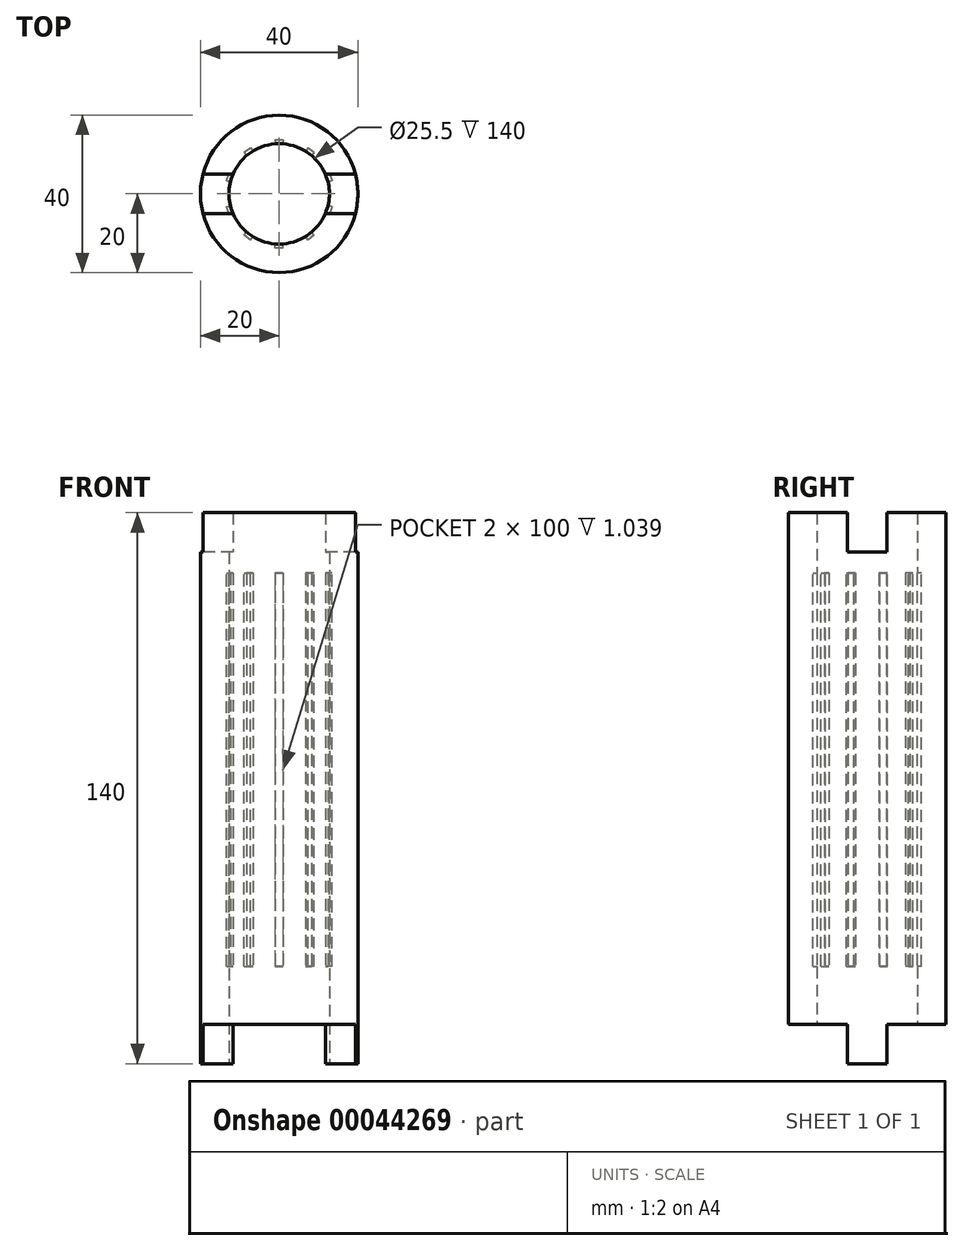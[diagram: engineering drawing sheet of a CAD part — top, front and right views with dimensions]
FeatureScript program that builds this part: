
annotation { "Feature Type Name" : "Feature", "Feature Type Description" : "" }
export const myFeature = defineFeature(function(context is Context, id is Id, definition is map)
    precondition{}
    {
        {
            var Q0;
            Q0=qCreatedBy(makeId("Top.planeOp"),FACE);
            var sketch = newSketch(context, id + "F0", { "sketchPlane" : qUnion([Q0])});
            skCircle(sketch, "E0", {"center": v(0, 0) * mm, "radius": 20 * mm});
            skCircle(sketch, "E1", {"center": v(0, 0) * mm, "radius": 12.75 * mm});
            skSolve(sketch);
        }
        {
            var Q0;
            Q0=makeQuery(id+"F0.imprint","IMPRINT",FACE,{"disambiguationData":[TD([[makeQuery(id+"F0.imprint","IMPRINT",EDGE,{"derivedFrom":sQuery(id+"F0.wireOp",EDGE,"E0")}),1.0]])]});
            var Q1;
            Q1=sQuery(id+"F0.wireOp",EDGE,"E0");
            extrude(context, id + "F1", {"entities" : qUnion([Q0]), "surfaceEntities" : qUnion([Q1]), "endBound" : BoundingType.SYMMETRIC, "depth" : 200 * mm});
        }
        {
            var Q0;
            Q0=qCreatedBy(makeId("Right.planeOp"),FACE);
            var sketch = newSketch(context, id + "F2", { "sketchPlane" : qUnion([Q0])});
            skLineSegment(sketch, "E2.bottom", {"start": v(-30, 65.34) * mm, "end": v(-5, 65.34) * mm});
            skLineSegment(sketch, "E2.top", {"start": v(-30, -64.66) * mm, "end": v(-5, -64.66) * mm});
            skLineSegment(sketch, "E2.left", {"start": v(-30, 65.34) * mm, "end": v(-30, -64.66) * mm});
            skLineSegment(sketch, "E2.right", {"start": v(30, 65.34) * mm, "end": v(30, -64.66) * mm});
            skLineSegment(sketch, "E3.top", {"start": v(-5, -74.66) * mm, "end": v(5, -74.66) * mm});
            skLineSegment(sketch, "E3.left", {"start": v(-5, -64.66) * mm, "end": v(-5, -74.66) * mm});
            skLineSegment(sketch, "E3.right", {"start": v(5, -64.66) * mm, "end": v(5, -74.66) * mm});
            skLineSegment(sketch, "E4.top", {"start": v(5, 55.34) * mm, "end": v(-5, 55.34) * mm});
            skLineSegment(sketch, "E4.left", {"start": v(5, 65.34) * mm, "end": v(5, 55.34) * mm});
            skLineSegment(sketch, "E4.right", {"start": v(-5, 65.34) * mm, "end": v(-5, 55.34) * mm});
            skLineSegment(sketch, "E5.trimOffspring", {"start": v(5, 65.34) * mm, "end": v(30, 65.34) * mm});
            skLineSegment(sketch, "E6.trimOffspring", {"start": v(5, -64.66) * mm, "end": v(30, -64.66) * mm});
            skSolve(sketch);
        }
        {
            var Q0;
            Q0=makeQuery(id+"F2.imprint","IMPRINT",FACE,{"disambiguationData":[TD([[makeQuery(id+"F2.imprint","IMPRINT",EDGE,{"derivedFrom":sQuery(id+"F2.wireOp",EDGE,"E2.bottom")}),-1.0]])]});
            extrude(context, id + "F3", {"entities" : qUnion([Q0]), "operationType" : NewBodyOperationType.INTERSECT, "endBound" : BoundingType.SYMMETRIC, "depth" : 50 * mm});
        }
        {
            var Q0;
            Q0=qCreatedBy(makeId("Top.planeOp"),FACE);
            var sketch = newSketch(context, id + "F4", { "sketchPlane" : qUnion([Q0])});
            skLineSegment(sketch, "E7.bottom", {"start": v(-1, 13.75) * mm, "end": v(1, 13.75) * mm});
            skLineSegment(sketch, "E7.top", {"start": v(-1, 11.75) * mm, "end": v(1, 11.75) * mm});
            skLineSegment(sketch, "E7.left", {"start": v(-1, 13.75) * mm, "end": v(-1, 11.75) * mm});
            skLineSegment(sketch, "E7.right", {"start": v(1, 13.75) * mm, "end": v(1, 11.75) * mm});
            skLineSegment(sketch, "E8.1.0", {"start": v(-7.27, 11.71) * mm, "end": v(-6.1, 10.1) * mm});
            skLineSegment(sketch, "E8.1.1", {"start": v(-8.9, 10.54) * mm, "end": v(-7.27, 11.71) * mm});
            skLineSegment(sketch, "E8.1.2", {"start": v(-8.9, 10.54) * mm, "end": v(-7.72, 8.92) * mm});
            skLineSegment(sketch, "E8.1.3", {"start": v(-7.72, 8.92) * mm, "end": v(-6.1, 10.1) * mm});
            skLineSegment(sketch, "E8.2.0", {"start": v(-12.77, 5.2) * mm, "end": v(-10.87, 4.58) * mm});
            skLineSegment(sketch, "E8.2.1", {"start": v(-13.39, 3.3) * mm, "end": v(-12.77, 5.2) * mm});
            skLineSegment(sketch, "E8.2.2", {"start": v(-13.39, 3.3) * mm, "end": v(-11.48, 2.68) * mm});
            skLineSegment(sketch, "E8.2.3", {"start": v(-11.48, 2.68) * mm, "end": v(-10.87, 4.58) * mm});
            skLineSegment(sketch, "E8.3.0", {"start": v(-13.39, -3.3) * mm, "end": v(-11.48, -2.68) * mm});
            skLineSegment(sketch, "E8.3.1", {"start": v(-12.77, -5.2) * mm, "end": v(-13.39, -3.3) * mm});
            skLineSegment(sketch, "E8.3.2", {"start": v(-12.77, -5.2) * mm, "end": v(-10.87, -4.58) * mm});
            skLineSegment(sketch, "E8.3.3", {"start": v(-10.87, -4.58) * mm, "end": v(-11.48, -2.68) * mm});
            skLineSegment(sketch, "E8.4.0", {"start": v(-8.9, -10.54) * mm, "end": v(-7.72, -8.92) * mm});
            skLineSegment(sketch, "E8.4.1", {"start": v(-7.27, -11.71) * mm, "end": v(-8.9, -10.54) * mm});
            skLineSegment(sketch, "E8.4.2", {"start": v(-7.27, -11.71) * mm, "end": v(-6.1, -10.1) * mm});
            skLineSegment(sketch, "E8.4.3", {"start": v(-6.1, -10.1) * mm, "end": v(-7.72, -8.92) * mm});
            skLineSegment(sketch, "E8.5.0", {"start": v(-1, -13.75) * mm, "end": v(-1, -11.75) * mm});
            skLineSegment(sketch, "E8.5.1", {"start": v(1, -13.75) * mm, "end": v(-1, -13.75) * mm});
            skLineSegment(sketch, "E8.5.2", {"start": v(1, -13.75) * mm, "end": v(1, -11.75) * mm});
            skLineSegment(sketch, "E8.5.3", {"start": v(1, -11.75) * mm, "end": v(-1, -11.75) * mm});
            skLineSegment(sketch, "E8.6.0", {"start": v(7.27, -11.71) * mm, "end": v(6.1, -10.1) * mm});
            skLineSegment(sketch, "E8.6.1", {"start": v(8.9, -10.54) * mm, "end": v(7.27, -11.71) * mm});
            skLineSegment(sketch, "E8.6.2", {"start": v(8.9, -10.54) * mm, "end": v(7.72, -8.92) * mm});
            skLineSegment(sketch, "E8.6.3", {"start": v(7.72, -8.92) * mm, "end": v(6.1, -10.1) * mm});
            skLineSegment(sketch, "E8.7.0", {"start": v(12.77, -5.2) * mm, "end": v(10.87, -4.58) * mm});
            skLineSegment(sketch, "E8.7.1", {"start": v(13.39, -3.3) * mm, "end": v(12.77, -5.2) * mm});
            skLineSegment(sketch, "E8.7.2", {"start": v(13.39, -3.3) * mm, "end": v(11.48, -2.68) * mm});
            skLineSegment(sketch, "E8.7.3", {"start": v(11.48, -2.68) * mm, "end": v(10.87, -4.58) * mm});
            skLineSegment(sketch, "E8.8.0", {"start": v(13.39, 3.3) * mm, "end": v(11.48, 2.68) * mm});
            skLineSegment(sketch, "E8.8.1", {"start": v(12.77, 5.2) * mm, "end": v(13.39, 3.3) * mm});
            skLineSegment(sketch, "E8.8.2", {"start": v(12.77, 5.2) * mm, "end": v(10.87, 4.58) * mm});
            skLineSegment(sketch, "E8.8.3", {"start": v(10.87, 4.58) * mm, "end": v(11.48, 2.68) * mm});
            skLineSegment(sketch, "E8.9.0", {"start": v(8.9, 10.54) * mm, "end": v(7.72, 8.92) * mm});
            skLineSegment(sketch, "E8.9.1", {"start": v(7.27, 11.71) * mm, "end": v(8.9, 10.54) * mm});
            skLineSegment(sketch, "E8.9.2", {"start": v(7.27, 11.71) * mm, "end": v(6.1, 10.1) * mm});
            skLineSegment(sketch, "E8.9.3", {"start": v(6.1, 10.1) * mm, "end": v(7.72, 8.92) * mm});
            skPoint(sketch, "E8.center", {"position": v(0, 0) * mm});
            skSolve(sketch);
        }
        {
            var Q0;
            Q0=qSketchRegion(id+"F4",true);
            extrude(context, id + "F5", {"entities" : qUnion([Q0]), "operationType" : NewBodyOperationType.REMOVE, "endBound" : BoundingType.SYMMETRIC, "oppositeDirection" : true, "depth" : 100 * mm});
        }
    });
